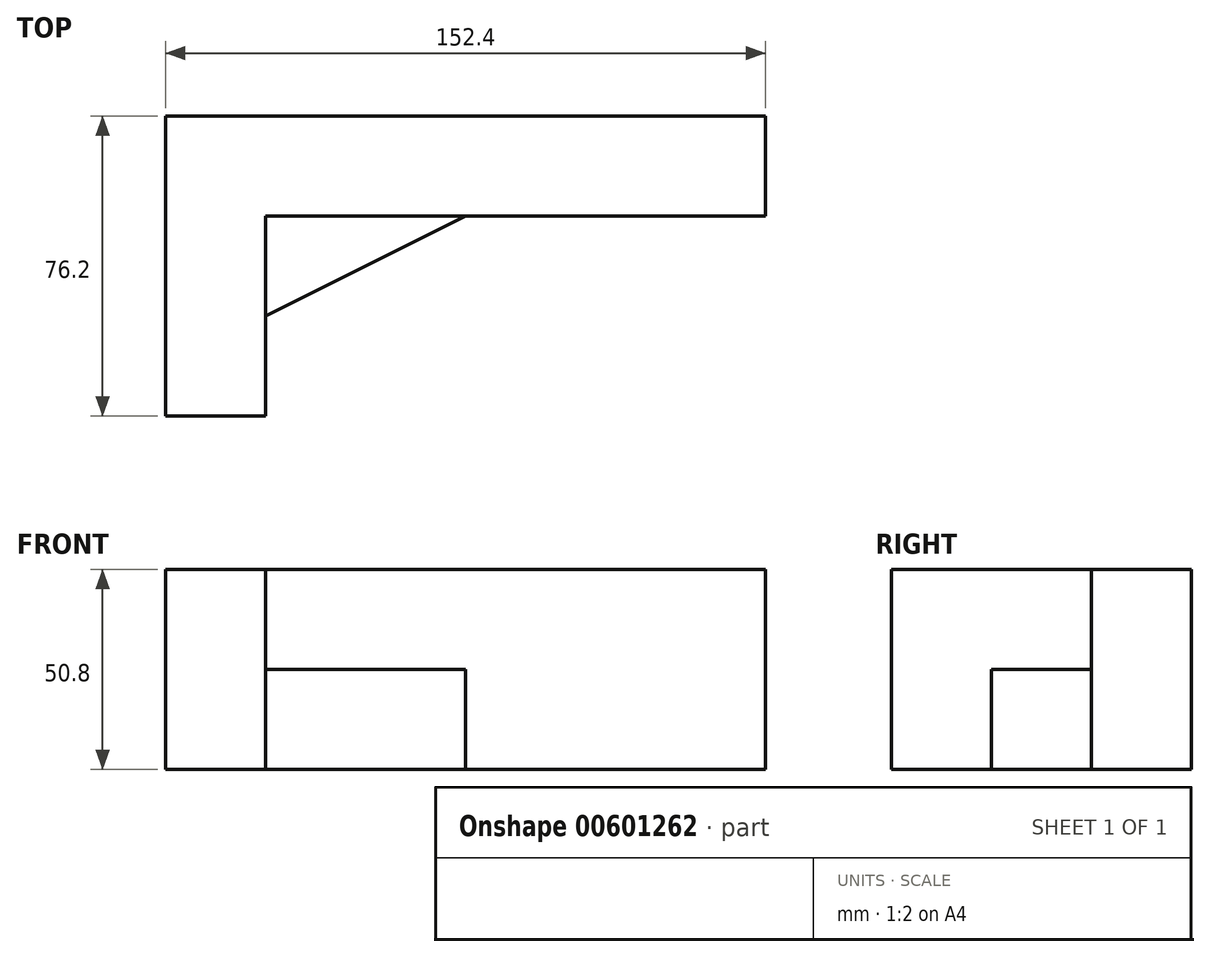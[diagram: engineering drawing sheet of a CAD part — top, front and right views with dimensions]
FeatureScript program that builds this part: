
annotation { "Feature Type Name" : "Feature", "Feature Type Description" : "" }
export const myFeature = defineFeature(function(context is Context, id is Id, definition is map)
    precondition{}
    {
        {
            var Q0;
            Q0=qCreatedBy(makeId("Front.planeOp"),FACE);
            var sketch = newSketch(context, id + "F0", { "sketchPlane" : qUnion([Q0])});
            skLineSegment(sketch, "E0.bottom", {"start": v(0, 0) * mm, "end": v(152.4, 0) * mm});
            skLineSegment(sketch, "E0.top", {"start": v(0, 50.8) * mm, "end": v(152.4, 50.8) * mm});
            skLineSegment(sketch, "E0.left", {"start": v(0, 0) * mm, "end": v(0, 50.8) * mm});
            skLineSegment(sketch, "E0.right", {"start": v(152.4, 0) * mm, "end": v(152.4, 50.8) * mm});
            skSolve(sketch);
        }
        {
            var Q0;
            Q0=qSketchRegion(id+"F0",true);
            extrude(context, id + "F1", {"entities" : qUnion([Q0]), "oppositeDirection" : true, "depth" : 76.2 * mm, "offsetDistance" : 25.4 * mm});
        }
        {
            var Q0;
            Q0=makeQuery(id+"F1.opExtrude","CAP_FACE",FACE,{"disambiguationData":[OSD([sQuery(id+"F0.wireOp",EDGE,"E0.bottom"),sQuery(id+"F0.wireOp",EDGE,"E0.top"),sQuery(id+"F0.wireOp",EDGE,"E0.left"),sQuery(id+"F0.wireOp",EDGE,"E0.right")])],"isStart":true});
            var sketch = newSketch(context, id + "F2", { "sketchPlane" : qUnion([Q0])});
            skLineSegment(sketch, "E1", {"start": v(0, 50.8) * mm, "end": v(25.4, 50.8) * mm});
            skLineSegment(sketch, "E2", {"start": v(25.4, 50.8) * mm, "end": v(25.4, 0) * mm});
            skLineSegment(sketch, "E3", {"start": v(25.4, 0) * mm, "end": v(0, 0) * mm});
            skLineSegment(sketch, "E4", {"start": v(0, 0) * mm, "end": v(0, 50.8) * mm});
            skLineSegment(sketch, "E5", {"start": v(25.4, 50.8) * mm, "end": v(152.4, 50.8) * mm});
            skLineSegment(sketch, "E6", {"start": v(152.4, 50.8) * mm, "end": v(152.4, 0) * mm});
            skLineSegment(sketch, "E7", {"start": v(152.4, 0) * mm, "end": v(76.2, 0) * mm});
            skLineSegment(sketch, "E8", {"start": v(76.2, 0) * mm, "end": v(76.2, 25.4) * mm});
            skLineSegment(sketch, "E9", {"start": v(76.2, 25.4) * mm, "end": v(25.4, 25.4) * mm});
            skSolve(sketch);
        }
        {
            var Q0;
            {var subQ0=sQuery(id+"F2.wireOp",EDGE,"E5");Q0=makeQuery(id+"F2.imprint","IMPRINT",FACE,{"disambiguationData":[TD([[makeQuery(id+"F2.imprint","IMPRINT",EDGE,{"derivedFrom":subQ0}),-1.0]])]});}
            extrude(context, id + "F3", {"entities" : qUnion([Q0]), "operationType" : NewBodyOperationType.REMOVE, "oppositeDirection" : true, "depth" : 50.8 * mm, "offsetDistance" : 25.4 * mm});
        }
        {
            var Q0;
            Q0=makeQuery(id+"F3.boolean.opBoolean","COPY",FACE,{"derivedFrom":makeQuery(id+"F3.opExtrude","SWEPT_FACE",FACE,{"disambiguationData":[OSD([sQuery(id+"F2.wireOp",EDGE,"E9")])]})});
            var sketch = newSketch(context, id + "F4", { "sketchPlane" : qUnion([Q0])});
            skLineSegment(sketch, "E10", {"start": v(25.4, 0) * mm, "end": v(25.4, 25.4) * mm});
            skLineSegment(sketch, "E11", {"start": v(25.4, 25.4) * mm, "end": v(76.2, 50.8) * mm});
            skLineSegment(sketch, "E12", {"start": v(76.2, 50.8) * mm, "end": v(25.4, 50.8) * mm});
            skLineSegment(sketch, "E13", {"start": v(25.4, 50.8) * mm, "end": v(25.4, 25.4) * mm});
            skSolve(sketch);
        }
        {
            var Q0;
            Q0=makeQuery(id+"F4.imprint","IMPRINT",FACE,{"disambiguationData":[TD([[makeQuery(id+"F4.imprint","IMPRINT",EDGE,{"derivedFrom":sQuery(id+"F4.wireOp",EDGE,"E10")}),1.0]])]});
            extrude(context, id + "F5", {"entities" : qUnion([Q0]), "operationType" : NewBodyOperationType.REMOVE, "oppositeDirection" : true, "depth" : 25.4 * mm, "offsetDistance" : 25.4 * mm});
        }
    });
